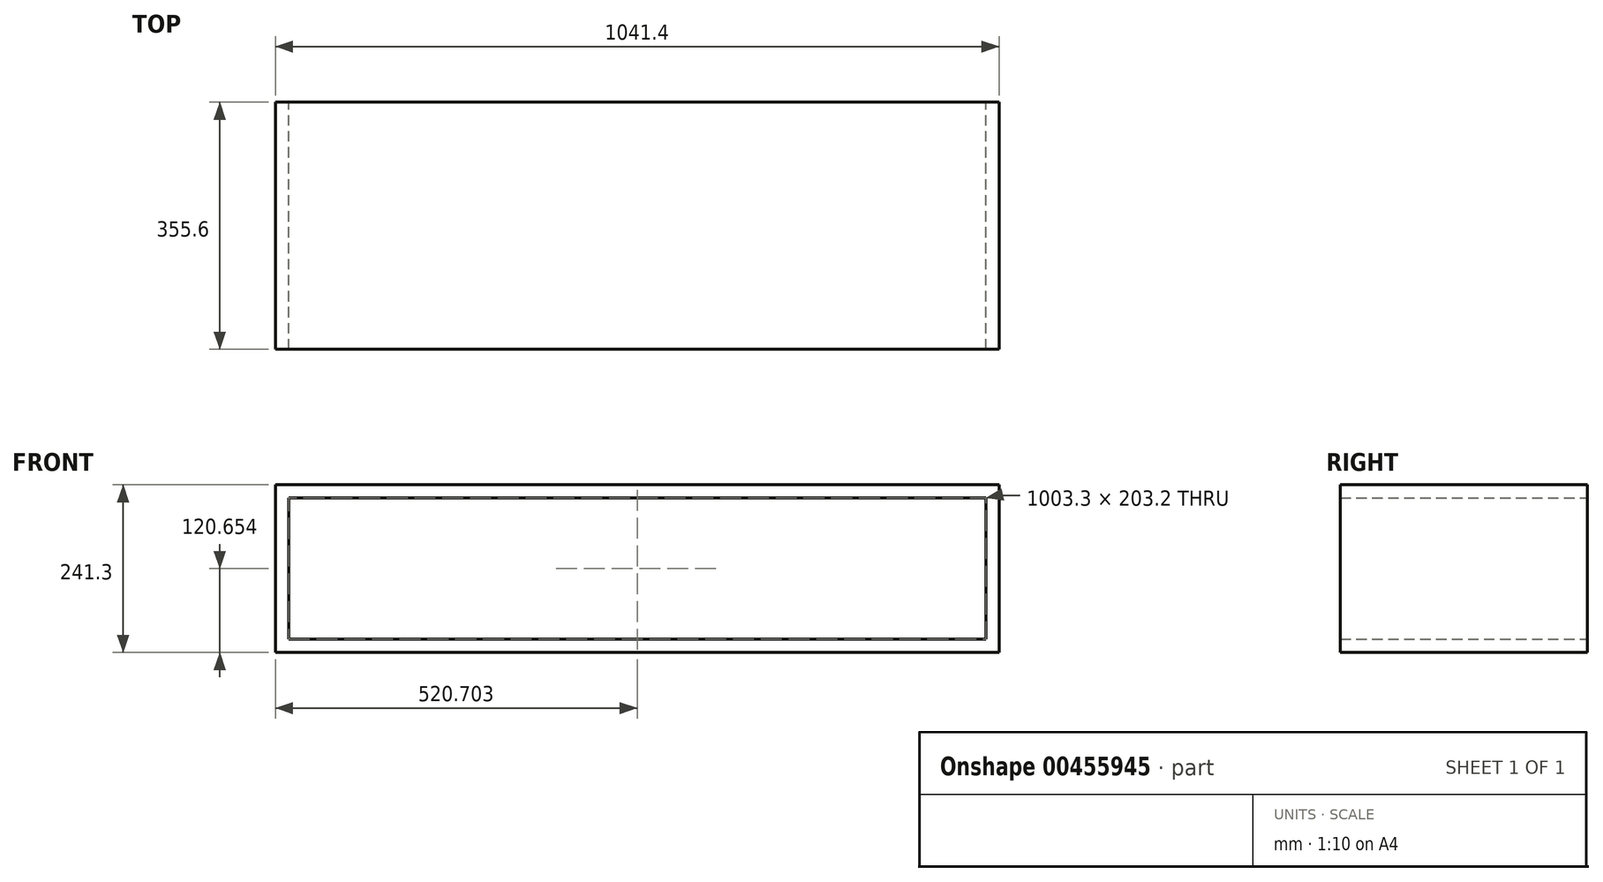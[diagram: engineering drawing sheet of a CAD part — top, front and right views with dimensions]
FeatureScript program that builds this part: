
annotation { "Feature Type Name" : "Feature", "Feature Type Description" : "" }
export const myFeature = defineFeature(function(context is Context, id is Id, definition is map)
    precondition{}
    {
        {
            var Q0;
            Q0=qCreatedBy(makeId("Front.planeOp"),FACE);
            var sketch = newSketch(context, id + "F0", { "sketchPlane" : qUnion([Q0])});
            skLineSegment(sketch, "E0.bottom", {"start": v(-503.4, -9.7) * mm, "end": v(538, -9.7) * mm});
            skLineSegment(sketch, "E0.top", {"start": v(-503.4, -251) * mm, "end": v(538, -251) * mm});
            skLineSegment(sketch, "E0.left", {"start": v(-503.4, -9.7) * mm, "end": v(-503.4, -251) * mm});
            skLineSegment(sketch, "E0.right", {"start": v(538, -9.7) * mm, "end": v(538, -251) * mm});
            skLineSegment(sketch, "E1", {"start": v(-503.4, -9.7) * mm, "end": v(-484.36, -9.7) * mm, "construction": true});
            skLineSegment(sketch, "E2", {"start": v(-484.36, -9.7) * mm, "end": v(-484.36, -28.76) * mm, "construction": true});
            skLineSegment(sketch, "E3", {"start": v(538, -251) * mm, "end": v(518.94, -251) * mm, "construction": true});
            skLineSegment(sketch, "E4", {"start": v(518.94, -251) * mm, "end": v(518.94, -231.96) * mm, "construction": true});
            skLineSegment(sketch, "E5.bottom", {"start": v(-484.36, -28.76) * mm, "end": v(518.94, -28.76) * mm});
            skLineSegment(sketch, "E5.top", {"start": v(-484.36, -231.96) * mm, "end": v(518.94, -231.96) * mm});
            skLineSegment(sketch, "E5.left", {"start": v(-484.36, -28.76) * mm, "end": v(-484.36, -231.96) * mm});
            skLineSegment(sketch, "E5.right", {"start": v(518.94, -28.76) * mm, "end": v(518.94, -231.96) * mm});
            skSolve(sketch);
        }
        {
            var Q0;
            Q0=makeQuery(id+"F0.imprint","IMPRINT",FACE,{"disambiguationData":[TD([[makeQuery(id+"F0.imprint","IMPRINT",EDGE,{"derivedFrom":sQuery(id+"F0.wireOp",EDGE,"E0.bottom")}),-1.0]])]});
            extrude(context, id + "F1", {"entities" : qUnion([Q0]), "depth" : 355.6 * mm, "offsetDistance" : 25.4 * mm});
        }
    });
